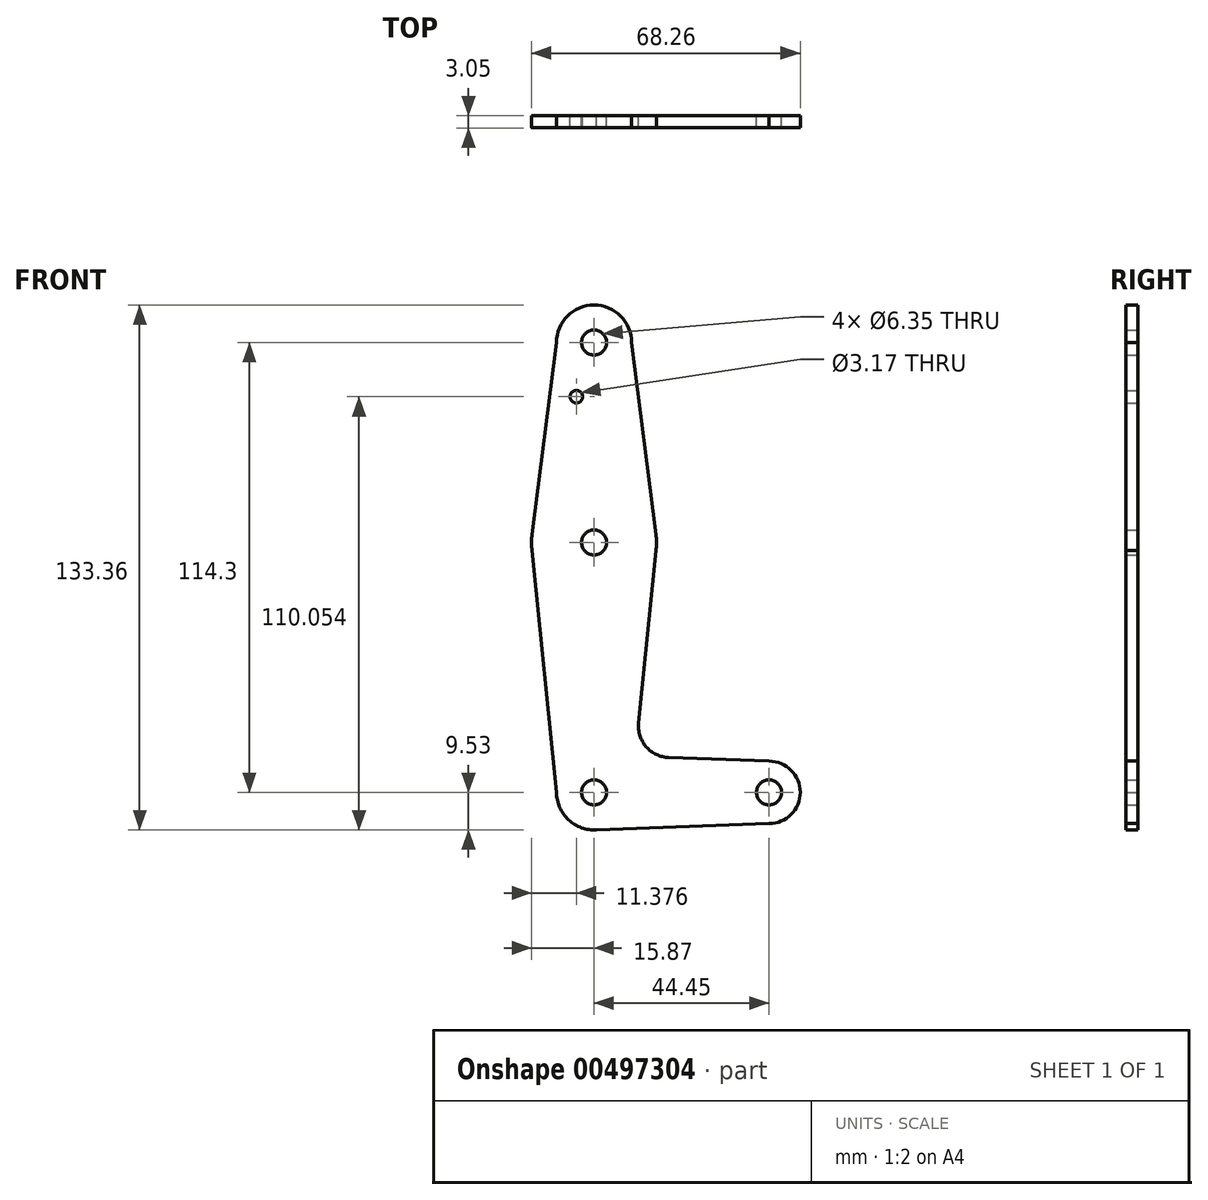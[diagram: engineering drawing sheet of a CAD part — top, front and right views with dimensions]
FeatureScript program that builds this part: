
annotation { "Feature Type Name" : "Feature", "Feature Type Description" : "" }
export const myFeature = defineFeature(function(context is Context, id is Id, definition is map)
    precondition{}
    {
        {
            var Q0;
            Q0=qCreatedBy(makeId("Front.planeOp"),FACE);
            var sketch = newSketch(context, id + "F0", { "sketchPlane" : qUnion([Q0])});
            skLineSegment(sketch, "E0", {"start": v(0, 0) * mm, "end": v(44.45, 0) * mm, "construction": true});
            skLineSegment(sketch, "E1", {"start": v(0, 0) * mm, "end": v(0, 114.3) * mm, "construction": true});
            skCircle(sketch, "E2", {"center": v(0, 114.3) * mm, "radius": 9.53 * mm});
            skCircle(sketch, "E3", {"center": v(0, 63.5) * mm, "radius": 15.88 * mm});
            skCircle(sketch, "E4", {"center": v(0, 0) * mm, "radius": 9.53 * mm});
            skCircle(sketch, "E5", {"center": v(44.45, 0) * mm, "radius": 7.94 * mm});
            skLineSegment(sketch, "E6", {"start": v(-9.53, 114.3) * mm, "end": v(-15.75, 65.5) * mm});
            skLineSegment(sketch, "E7", {"start": v(9.53, 114.3) * mm, "end": v(15.75, 65.5) * mm});
            skLineSegment(sketch, "E8", {"start": v(-15.75, 61.5) * mm, "end": v(-9.53, 0) * mm});
            skLineSegment(sketch, "E9", {"start": v(15.75, 61.5) * mm, "end": v(11.34, 17.59) * mm});
            skLineSegment(sketch, "E10", {"start": v(18.97, 8.85) * mm, "end": v(44.45, 7.94) * mm});
            skLineSegment(sketch, "E11", {"start": v(0, -9.52) * mm, "end": v(44.45, -7.94) * mm});
            skCircle(sketch, "E12", {"center": v(0, 114.3) * mm, "radius": 3.18 * mm});
            skCircle(sketch, "E13", {"center": v(0, 63.5) * mm, "radius": 3.18 * mm});
            skCircle(sketch, "E14", {"center": v(0, 0) * mm, "radius": 3.18 * mm});
            skCircle(sketch, "E15", {"center": v(44.45, 0) * mm, "radius": 3.18 * mm});
            skCircle(sketch, "E16", {"center": v(-4.5, 100.52) * mm, "radius": 1.59 * mm});
            skArc(sketch, "E17.filletArc", {"start": v(11.34, 17.59) * mm, "mid": v(13.26, 11.57) * mm, "end": v(18.97, 8.85) * mm});
            skSolve(sketch);
        }
        {
            var Q0;
            Q0 = qSketchRegion(id + "F0", true);
            extrude(context, id + "F1", {"entities" : qUnion([Q0]), "depth" : 3.05 * mm, "offsetDistance" : 25.4 * mm});
        }
    });
